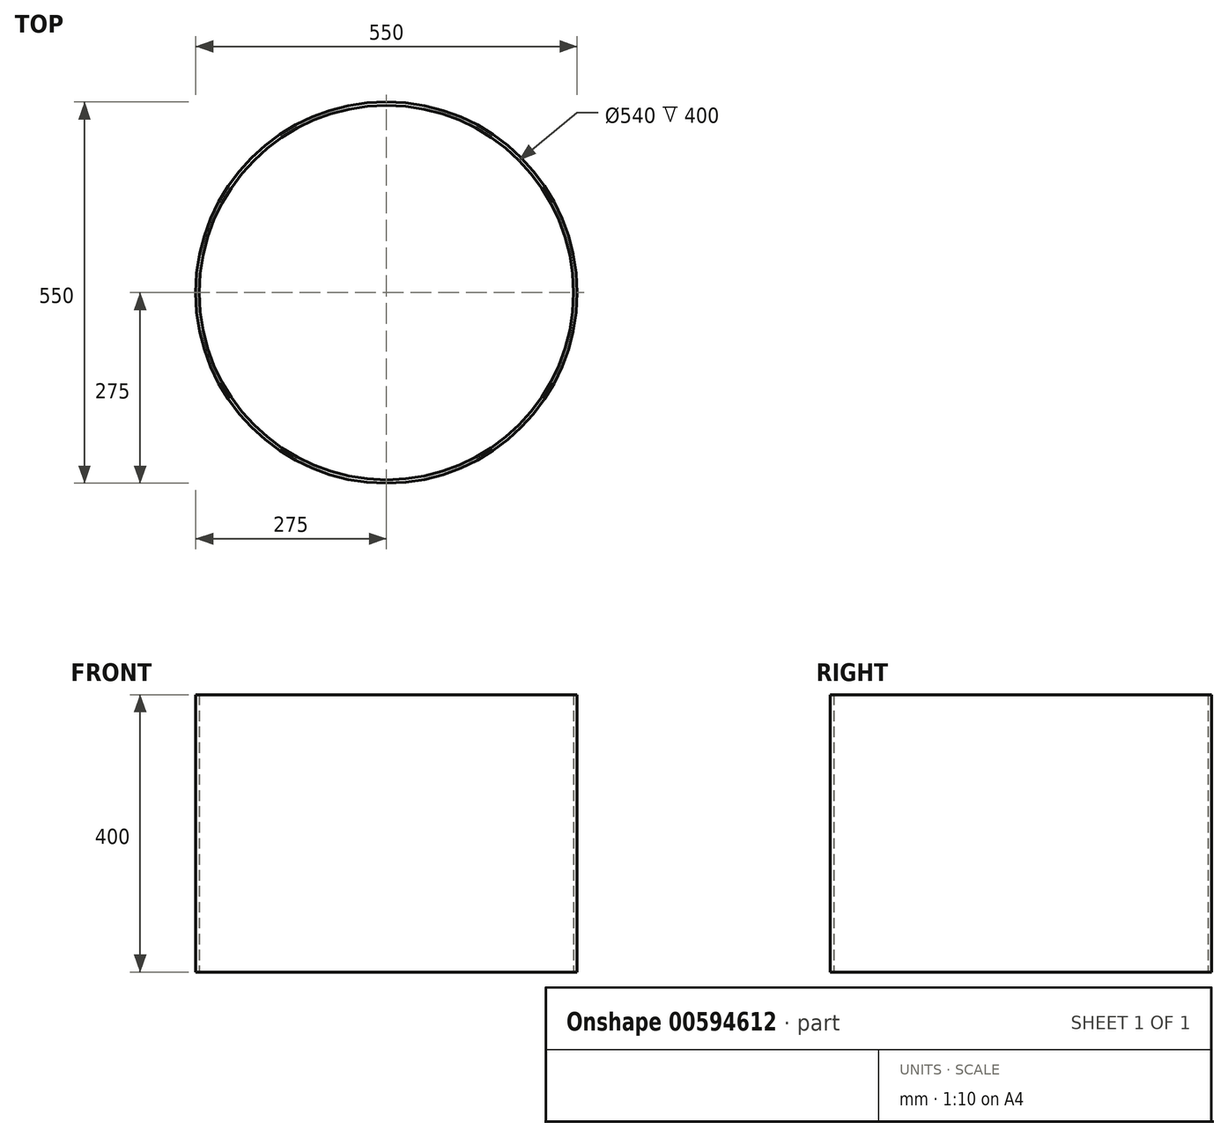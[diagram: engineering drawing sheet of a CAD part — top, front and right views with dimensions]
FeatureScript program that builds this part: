
annotation { "Feature Type Name" : "Feature", "Feature Type Description" : "" }
export const myFeature = defineFeature(function(context is Context, id is Id, definition is map)
    precondition{}
    {
        {
            var Q0;
            Q0=qCreatedBy(makeId("Top.planeOp"),FACE);
            var sketch = newSketch(context, id + "F0", { "sketchPlane" : qUnion([Q0])});
            skCircle(sketch, "E0", {"center": v(0, 0) * mm, "radius": 275 * mm});
            skCircle(sketch, "E1", {"center": v(0, 0) * mm, "radius": 270 * mm});
            skSolve(sketch);
        }
        {
            var Q0;
            Q0=makeQuery(id+"F0.imprint","IMPRINT",FACE,{"disambiguationData":[TD([[makeQuery(id+"F0.imprint","IMPRINT",EDGE,{"derivedFrom":sQuery(id+"F0.wireOp",EDGE,"E0")}),1.0]])]});
            extrude(context, id + "F1", {"entities" : qUnion([Q0]), "depth" : 400 * mm, "offsetDistance" : 25 * mm});
        }
    });
